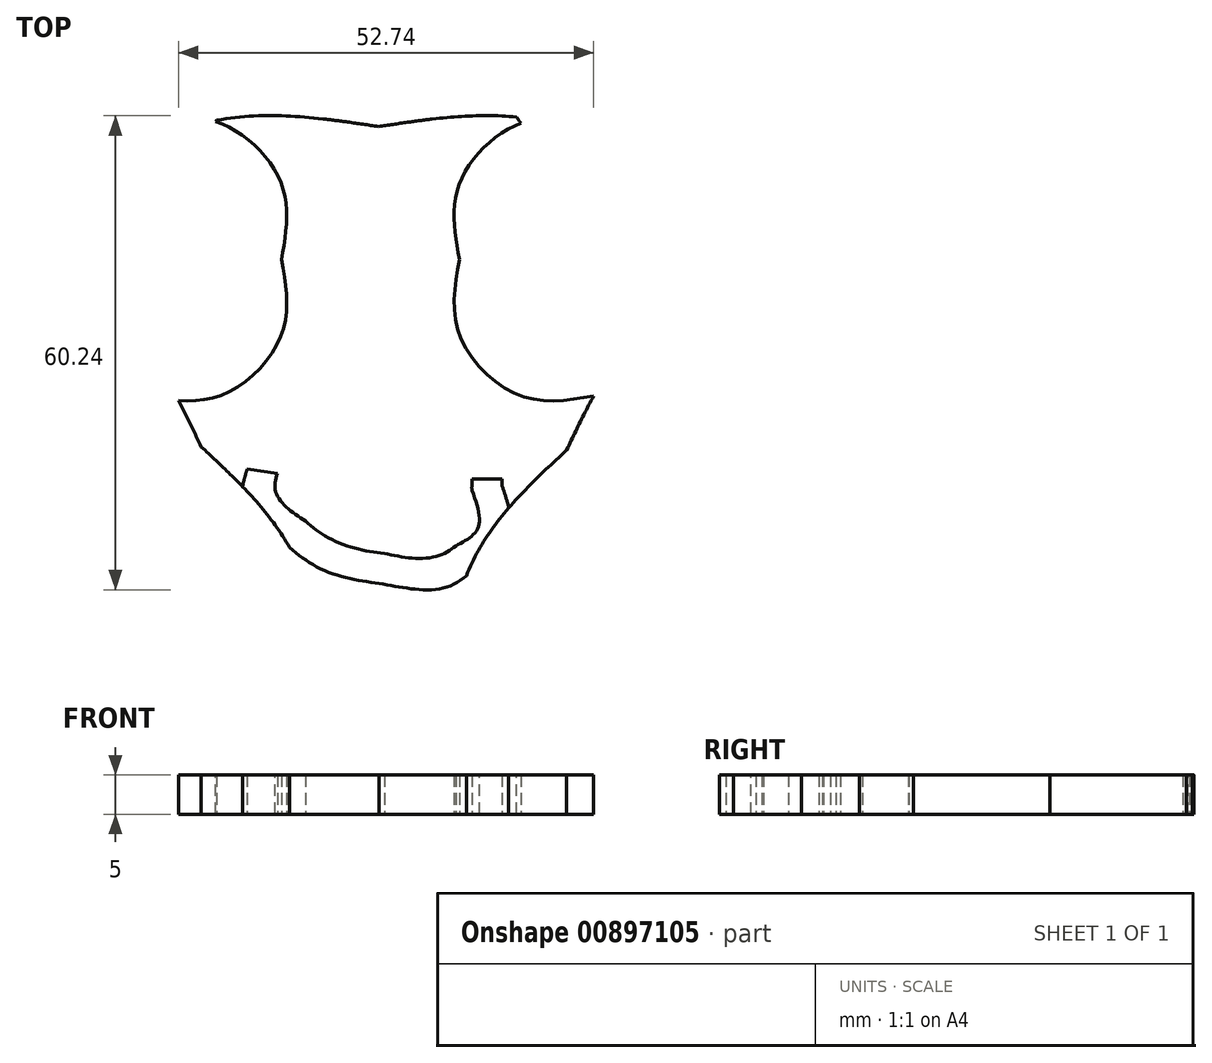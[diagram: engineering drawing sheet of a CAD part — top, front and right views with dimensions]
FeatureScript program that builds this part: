
annotation { "Feature Type Name" : "Feature", "Feature Type Description" : "" }
export const myFeature = defineFeature(function(context is Context, id is Id, definition is map)
    precondition{}
    {
        {
            var Q0;
            Q0=qCreatedBy(makeId("Top.planeOp"),FACE);
            var sketch = newSketch(context, id + "F0", { "sketchPlane" : qUnion([Q0])});
            skLineSegment(sketch, "E0", {"start": v(-46.86, -8.88) * mm, "end": v(-46.86, -8.8) * mm});
            skLineSegment(sketch, "E1", {"start": v(-65.14, 32.5) * mm, "end": v(-66.9, 31.52) * mm});
            skLineSegment(sketch, "E2", {"start": v(-116.84, 62) * mm, "end": v(-116.62, 62.31) * mm});
            skLineSegment(sketch, "E3", {"start": v(-116.62, 62.31) * mm, "end": v(-116.84, 62) * mm});
            skLineSegment(sketch, "E4", {"start": v(-68.87, 38.19) * mm, "end": v(-85.8, 24.7) * mm});
            skLineSegment(sketch, "E5", {"start": v(-85.8, 24.7) * mm, "end": v(-81.78, 19.66) * mm});
            skLineSegment(sketch, "E6", {"start": v(-81.78, 19.66) * mm, "end": v(-66.9, 31.52) * mm});
            skLineSegment(sketch, "E7", {"start": v(16.61, -28.9) * mm, "end": v(16.61, -28.02) * mm});
            skLineSegment(sketch, "E8", {"start": v(16.61, -28.02) * mm, "end": v(12.75, -28.02) * mm});
            skLineSegment(sketch, "E9", {"start": v(-11.95, -27.29) * mm, "end": v(-15.77, -26.73) * mm});
            skLineSegment(sketch, "E10", {"start": v(-15.77, -26.73) * mm, "end": v(-11.95, -27.29) * mm});
            skLineSegment(sketch, "E11", {"start": v(-14.67, 45.1) * mm, "end": v(-11.05, 44.39) * mm});
            skLineSegment(sketch, "E12", {"start": v(-11.05, 44.39) * mm, "end": v(-10.47, 47.34) * mm});
            skLineSegment(sketch, "E13", {"start": v(-10.47, 47.34) * mm, "end": v(-12, 47.64) * mm});
            skLineSegment(sketch, "E14", {"start": v(-12, 47.64) * mm, "end": v(-9.9, 51.16) * mm});
            skLineSegment(sketch, "E15", {"start": v(-9.9, 51.16) * mm, "end": v(-7.44, 45.28) * mm});
            skLineSegment(sketch, "E16", {"start": v(-4.7, 46.53) * mm, "end": v(-4.66, 46.45) * mm});
            skLineSegment(sketch, "E17", {"start": v(-4.66, 46.45) * mm, "end": v(-4.7, 46.53) * mm});
            skLineSegment(sketch, "E18", {"start": v(9.82, 55.07) * mm, "end": v(6.2, 46.45) * mm});
            skLineSegment(sketch, "E19", {"start": v(6.2, 46.45) * mm, "end": v(6.23, 46.53) * mm});
            skLineSegment(sketch, "E20", {"start": v(6.23, 46.53) * mm, "end": v(9.82, 55.07) * mm});
            skLineSegment(sketch, "E21", {"start": v(8.97, 45.28) * mm, "end": v(11.44, 51.16) * mm});
            skLineSegment(sketch, "E22", {"start": v(11.44, 51.16) * mm, "end": v(13.53, 47.64) * mm});
            skLineSegment(sketch, "E23", {"start": v(13.53, 47.64) * mm, "end": v(12, 47.34) * mm});
            skLineSegment(sketch, "E24", {"start": v(12, 47.34) * mm, "end": v(12.58, 44.39) * mm});
            skLineSegment(sketch, "E25", {"start": v(12.58, 44.39) * mm, "end": v(16.2, 45.1) * mm});
            skLineSegment(sketch, "E26", {"start": v(17.2, 47.34) * mm, "end": v(12.5, 55.26) * mm});
            skLineSegment(sketch, "E27", {"start": v(12.5, 55.26) * mm, "end": v(17.2, 47.34) * mm});
            skLineSegment(sketch, "E28", {"start": v(-1.94, -75.4) * mm, "end": v(-1.94, -72.82) * mm});
            skLineSegment(sketch, "E29", {"start": v(-1.94, -72.82) * mm, "end": v(-1.22, -72.82) * mm});
            skLineSegment(sketch, "E30", {"start": v(-1.22, -72.82) * mm, "end": v(-6.78, -63.6) * mm});
            skLineSegment(sketch, "E31", {"start": v(-6.78, -63.6) * mm, "end": v(-6.78, -52.79) * mm});
            skLineSegment(sketch, "E32", {"start": v(4.46, -64.66) * mm, "end": v(10.59, -74.82) * mm});
            skLineSegment(sketch, "E33", {"start": v(11.69, -75.44) * mm, "end": v(11.69, -72.85) * mm});
            skLineSegment(sketch, "E34", {"start": v(11.69, -72.85) * mm, "end": v(12.4, -72.85) * mm});
            skLineSegment(sketch, "E35", {"start": v(12.4, -72.85) * mm, "end": v(6.84, -63.62) * mm});
            skLineSegment(sketch, "E36", {"start": v(6.84, -63.62) * mm, "end": v(6.84, -52.78) * mm});
            skLineSegment(sketch, "E37", {"start": v(59.65, 56.98) * mm, "end": v(70.61, 49.4) * mm});
            skLineSegment(sketch, "E38", {"start": v(60.06, 58.77) * mm, "end": v(60.06, 58.77) * mm});
            skLineSegment(sketch, "E39", {"start": v(73.56, 1.7) * mm, "end": v(73.56, 1.7) * mm});
            skLineSegment(sketch, "E40", {"start": v(84.95, 53.47) * mm, "end": v(62.16, 63) * mm});
            skLineSegment(sketch, "E41", {"start": v(62.16, 63) * mm, "end": v(59.65, 56.98) * mm});
            skLineSegment(sketch, "E42", {"start": v(87.28, 80.72) * mm, "end": v(87.28, 80.72) * mm});
            skLineSegment(sketch, "E43", {"start": v(121.59, 54.04) * mm, "end": v(121.59, 54.04) * mm});
            skLineSegment(sketch, "E44", {"start": v(118.71, 67.05) * mm, "end": v(118.71, 67.05) * mm});
            skLineSegment(sketch, "E45", {"start": v(110.57, 61.37) * mm, "end": v(110.57, 61.37) * mm});
            skFitSpline(sketch, "E46", {"points": [v(-34.7, -84.65) * mm, v(-55.4, -99.81) * mm, v(-83.07, -97.2) * mm, v(-96.56, -78.78) * mm]});
            skFitSpline(sketch, "E47", {"points": [v(-96.56, -78.78) * mm, v(-110, -60.4) * mm, v(-104.14, -33.21) * mm, v(-83.45, -18.08) * mm]});
            skFitSpline(sketch, "E48", {"points": [v(-21.63, -23.91) * mm, v(-8.14, -42.33) * mm, v(-14, -69.52) * mm, v(-34.7, -84.65) * mm]});
            skFitSpline(sketch, "E49", {"points": [v(-83.45, -18.08) * mm, v(-62.8, -2.92) * mm, v(-35.08, -5.53) * mm, v(-21.63, -23.91) * mm]});
            skFitSpline(sketch, "E50", {"points": [v(-29.88, 7.13) * mm, v(-46.62, -15.73) * mm, v(-81.06, -18.98) * mm, v(-106.76, -0.16) * mm]});
            skFitSpline(sketch, "E51", {"points": [v(-46.13, 82.62) * mm, v(-20.4, 63.8) * mm, v(-13.11, 29.99) * mm, v(-29.88, 7.13) * mm]});
            skFitSpline(sketch, "E52", {"points": [v(-106.76, -0.16) * mm, v(-132.5, 18.67) * mm, v(-139.78, 52.51) * mm, v(-123.04, 75.37) * mm]});
            skFitSpline(sketch, "E53", {"points": [v(-123.04, 75.37) * mm, v(-106.27, 98.23) * mm, v(-71.87, 101.48) * mm, v(-46.13, 82.62) * mm]});
            skFitSpline(sketch, "E54", {"points": [v(-69.89, 59.6) * mm, v(-60.89, 70.55) * mm, v(-45.8, 73.02) * mm, v(-36.16, 65.06) * mm]});
            skFitSpline(sketch, "E55", {"points": [v(-36.16, 65.06) * mm, v(-26.48, 57.14) * mm, v(-25.92, 41.87) * mm, v(-34.93, 30.92) * mm]});
            skFitSpline(sketch, "E56", {"points": [v(-34.93, 30.92) * mm, v(-43.9, 19.98) * mm, v(-58.98, 17.55) * mm, v(-68.66, 25.47) * mm]});
            skFitSpline(sketch, "E57", {"points": [v(-78, 61.63) * mm, v(-69, 72.57) * mm, v(-53.86, 75) * mm, v(-44.23, 67.08) * mm]});
            skFitSpline(sketch, "E58", {"points": [v(-44.23, 67.08) * mm, v(-34.55, 59.16) * mm, v(-34, 43.85) * mm, v(-43, 32.9) * mm]});
            skFitSpline(sketch, "E59", {"points": [v(-43, 32.9) * mm, v(-51.96, 21.96) * mm, v(-67.09, 19.53) * mm, v(-76.72, 27.45) * mm]});
            skFitSpline(sketch, "E60", {"points": [v(-82.96, 36.67) * mm, v(-91.85, 36.67) * mm, v(-99.06, 43.73) * mm, v(-99.06, 52.47) * mm]});
            skFitSpline(sketch, "E61", {"points": [v(-99.06, 52.47) * mm, v(-99.06, 61.22) * mm, v(-91.85, 68.28) * mm, v(-82.96, 68.28) * mm]});
            skFitSpline(sketch, "E62", {"points": [v(-82.96, 68.28) * mm, v(-74.07, 68.28) * mm, v(-66.86, 61.22) * mm, v(-66.86, 52.47) * mm]});
            skFitSpline(sketch, "E63", {"points": [v(-66.86, 52.47) * mm, v(-66.86, 43.73) * mm, v(-74.07, 36.67) * mm, v(-82.96, 36.67) * mm]});
            skFitSpline(sketch, "E64", {"points": [v(-82.96, 36.67) * mm, v(-91.85, 36.67) * mm, v(-99.06, 43.73) * mm, v(-99.06, 52.47) * mm]});
            skFitSpline(sketch, "E65", {"points": [v(-99.06, 52.47) * mm, v(-99.06, 61.22) * mm, v(-91.85, 68.28) * mm, v(-82.96, 68.28) * mm]});
            skFitSpline(sketch, "E66", {"points": [v(-82.96, 68.28) * mm, v(-74.07, 68.28) * mm, v(-66.86, 61.22) * mm, v(-66.86, 52.47) * mm]});
            skFitSpline(sketch, "E67", {"points": [v(-66.86, 52.47) * mm, v(-66.86, 43.73) * mm, v(-74.07, 36.67) * mm, v(-82.96, 36.67) * mm]});
            skFitSpline(sketch, "E68", {"points": [v(-75.8, 43.55) * mm, v(-79.11, 40.82) * mm, v(-84.08, 41.34) * mm, v(-86.88, 44.74) * mm]});
            skFitSpline(sketch, "E69", {"points": [v(-86.88, 44.74) * mm, v(-89.69, 48.14) * mm, v(-89.24, 53.1) * mm, v(-85.88, 55.84) * mm]});
            skFitSpline(sketch, "E70", {"points": [v(-85.88, 55.84) * mm, v(-82.55, 58.56) * mm, v(-77.58, 58.04) * mm, v(-74.82, 54.64) * mm]});
            skFitSpline(sketch, "E71", {"points": [v(-74.82, 54.64) * mm, v(-72.02, 51.24) * mm, v(-72.47, 46.27) * mm, v(-75.8, 43.55) * mm]});
            skFitSpline(sketch, "E72", {"points": [v(-75.8, 43.55) * mm, v(-79.11, 40.82) * mm, v(-84.08, 41.34) * mm, v(-86.88, 44.74) * mm]});
            skFitSpline(sketch, "E73", {"points": [v(-86.88, 44.74) * mm, v(-89.69, 48.14) * mm, v(-89.24, 53.1) * mm, v(-85.88, 55.84) * mm]});
            skFitSpline(sketch, "E74", {"points": [v(-85.88, 55.84) * mm, v(-82.55, 58.56) * mm, v(-77.58, 58.04) * mm, v(-74.82, 54.64) * mm]});
            skFitSpline(sketch, "E75", {"points": [v(-74.82, 54.64) * mm, v(-72.02, 51.24) * mm, v(-72.47, 46.27) * mm, v(-75.8, 43.55) * mm]});
            skFitSpline(sketch, "E76", {"points": [v(-102.83, 35.67) * mm, v(-109.7, 45.94) * mm, v(-117.51, 49.97) * mm, v(-109.3, 60.13) * mm]});
            skFitSpline(sketch, "E77", {"points": [v(-109.3, 60.13) * mm, v(-101.45, 69.73) * mm, v(-97.08, 80.04) * mm, v(-86.17, 81.76) * mm]});
            skFitSpline(sketch, "E78", {"points": [v(-56.55, 65.4) * mm, v(-57.45, 57.4) * mm, v(-54.76, 40.52) * mm, v(-65.14, 32.5) * mm]});
            skFitSpline(sketch, "E79", {"points": [v(-85.17, 83.6) * mm, v(-98.56, 83.6) * mm, v(-109.03, 74.4) * mm, v(-116.84, 62) * mm]});
            skFitSpline(sketch, "E80", {"points": [v(-116.62, 62.31) * mm, v(-119.13, 59.22) * mm, v(-120.2, 55.6) * mm, v(-120.12, 52.12) * mm]});
            skFitSpline(sketch, "E81", {"points": [v(-120.12, 52.12) * mm, v(-120.03, 48.64) * mm, v(-118.92, 45.3) * mm, v(-117.4, 42.11) * mm]});
            skFitSpline(sketch, "E82", {"points": [v(-117.4, 42.11) * mm, v(-114.34, 35.74) * mm, v(-109.54, 29.77) * mm, v(-106.22, 24.8) * mm]});
            skFitSpline(sketch, "E83", {"points": [v(-106.22, 24.8) * mm, v(-106.22, 24.8) * mm, v(-106.22, 24.8) * mm, v(-106.22, 24.8) * mm]});
            skFitSpline(sketch, "E84", {"points": [v(-106.22, 24.8) * mm, v(-100.9, 16.85) * mm, v(-91.9, 13.25) * mm, v(-82.78, 10.18) * mm]});
            skFitSpline(sketch, "E85", {"points": [v(-82.78, 10.18) * mm, v(-73.66, 7.1) * mm, v(-64.16, 4.52) * mm, v(-57, -0.26) * mm]});
            skFitSpline(sketch, "E86", {"points": [v(-53.42, 5.1) * mm, v(-61.83, 10.71) * mm, v(-71.89, 13.31) * mm, v(-80.73, 16.28) * mm]});
            skFitSpline(sketch, "E87", {"points": [v(-111.39, 58.56) * mm, v(-104.23, 69.93) * mm, v(-95.72, 77.05) * mm, v(-85.37, 77.15) * mm]});
            skFitSpline(sketch, "E88", {"points": [v(-85.37, 77.15) * mm, v(-79.56, 76.37) * mm, v(-73.73, 74.84) * mm, v(-69.2, 72.53) * mm]});
            skFitSpline(sketch, "E89", {"points": [v(-69.2, 72.53) * mm, v(-64.8, 70.28) * mm, v(-61.79, 67.42) * mm, v(-60.52, 63.9) * mm]});
            skFitSpline(sketch, "E90", {"points": [v(-60.52, 63.9) * mm, v(-61.3, 55.24) * mm, v(-60.15, 44.93) * mm, v(-68.83, 38.22) * mm]});
            skFitSpline(sketch, "E91", {"points": [v(-68.83, 38.22) * mm, v(-68.85, 38.2) * mm, v(-68.86, 38.2) * mm, v(-68.87, 38.19) * mm]});
            skFitSpline(sketch, "E92", {"points": [v(-64.9, 33.12) * mm, v(-53.08, 42.25) * mm, v(-54.83, 56.8) * mm, v(-54.06, 64.05) * mm]});
            skFitSpline(sketch, "E93", {"points": [v(-54.06, 64.05) * mm, v(-54.01, 64.48) * mm, v(-54.06, 64.93) * mm, v(-54.19, 65.34) * mm]});
            skFitSpline(sketch, "E94", {"points": [v(-54.19, 65.34) * mm, v(-56.02, 71.25) * mm, v(-60.72, 75.43) * mm, v(-66.26, 78.26) * mm]});
            skFitSpline(sketch, "E95", {"points": [v(-66.26, 78.26) * mm, v(-71.8, 81.1) * mm, v(-78.34, 82.73) * mm, v(-84.75, 83.57) * mm]});
            skFitSpline(sketch, "E96", {"points": [v(-84.75, 83.57) * mm, v(-84.89, 83.6) * mm, v(-85.03, 83.6) * mm, v(-85.17, 83.6) * mm]});
            skFitSpline(sketch, "E97", {"points": [v(-58.53, -0.23) * mm, v(-63.17, 2.42) * mm, v(-66, 6.12) * mm, v(-64.92, 8.02) * mm]});
            skFitSpline(sketch, "E98", {"points": [v(-64.92, 8.02) * mm, v(-63.8, 9.9) * mm, v(-59.2, 9.3) * mm, v(-54.57, 6.64) * mm]});
            skFitSpline(sketch, "E99", {"points": [v(-54.57, 6.64) * mm, v(-49.98, 3.95) * mm, v(-47.1, 0.3) * mm, v(-48.22, -1.61) * mm]});
            skFitSpline(sketch, "E100", {"points": [v(-48.22, -1.61) * mm, v(-49.3, -3.52) * mm, v(-53.94, -2.88) * mm, v(-58.53, -0.23) * mm]});
            skFitSpline(sketch, "E101", {"points": [v(24.8, -24.32) * mm, v(38.29, -5.9) * mm, v(65.96, -3.26) * mm, v(86.66, -18.42) * mm]});
            skFitSpline(sketch, "E102", {"points": [v(86.66, -18.42) * mm, v(107.31, -33.55) * mm, v(113.18, -60.78) * mm, v(99.7, -79.16) * mm]});
            skFitSpline(sketch, "E103", {"points": [v(99.7, -79.16) * mm, v(86.2, -97.57) * mm, v(58.53, -100.19) * mm, v(37.84, -85.06) * mm]});
            skFitSpline(sketch, "E104", {"points": [v(37.84, -85.06) * mm, v(17.18, -69.9) * mm, v(11.32, -42.7) * mm, v(24.8, -24.32) * mm]});
            skFitSpline(sketch, "E105", {"points": [v(0.9, -52.41) * mm, v(-23.01, -52.41) * mm, v(-42.36, -36.95) * mm, v(-42.36, -17.82) * mm]});
            skFitSpline(sketch, "E106", {"points": [v(-42.36, -17.82) * mm, v(-42.36, 1.26) * mm, v(-23.01, 16.77) * mm, v(0.9, 16.77) * mm]});
            skFitSpline(sketch, "E107", {"points": [v(0.9, 16.77) * mm, v(24.8, 16.77) * mm, v(44.15, 1.26) * mm, v(44.15, -17.82) * mm]});
            skFitSpline(sketch, "E108", {"points": [v(44.15, -17.82) * mm, v(44.15, -36.95) * mm, v(24.8, -52.41) * mm, v(0.9, -52.41) * mm]});
            skFitSpline(sketch, "E109", {"points": [v(-28.76, -17.41) * mm, v(-38.33, -17.41) * mm, v(-46.06, -9.64) * mm, v(-46.06, -0.12) * mm]});
            skFitSpline(sketch, "E110", {"points": [v(-46.06, -0.12) * mm, v(-46.06, 9.44) * mm, v(-38.33, 17.18) * mm, v(-28.76, 17.18) * mm]});
            skFitSpline(sketch, "E111", {"points": [v(-28.76, 17.18) * mm, v(-19.2, 17.18) * mm, v(-11.43, 9.44) * mm, v(-11.43, -0.12) * mm]});
            skFitSpline(sketch, "E112", {"points": [v(-11.43, -0.12) * mm, v(-11.43, -9.64) * mm, v(-19.2, -17.41) * mm, v(-28.76, -17.41) * mm]});
            skFitSpline(sketch, "E113", {"points": [v(-28.76, 15.67) * mm, v(-20.01, 15.67) * mm, v(-12.94, 8.63) * mm, v(-12.94, -0.12) * mm]});
            skFitSpline(sketch, "E114", {"points": [v(-12.94, -0.12) * mm, v(-12.94, -8.82) * mm, v(-20.02, -15.9) * mm, v(-28.76, -15.9) * mm]});
            skFitSpline(sketch, "E115", {"points": [v(-28.76, -15.9) * mm, v(-37.51, -15.9) * mm, v(-44.55, -8.83) * mm, v(-44.55, -0.12) * mm]});
            skFitSpline(sketch, "E116", {"points": [v(-44.55, -0.12) * mm, v(-44.55, 8.63) * mm, v(-37.51, 15.67) * mm, v(-28.76, 15.67) * mm]});
            skFitSpline(sketch, "E117", {"points": [v(30.55, 5) * mm, v(13.9, 27.7) * mm, v(21.14, 61.3) * mm, v(46.7, 80.04) * mm]});
            skFitSpline(sketch, "E118", {"points": [v(106.94, -2.25) * mm, v(81.4, -20.96) * mm, v(47.18, -17.71) * mm, v(30.55, 5) * mm]});
            skFitSpline(sketch, "E119", {"points": [v(30.55, 5) * mm, v(13.9, 27.7) * mm, v(21.14, 61.3) * mm, v(46.7, 80.04) * mm]});
            skFitSpline(sketch, "E120", {"points": [v(46.7, 80.04) * mm, v(72.24, 98.76) * mm, v(106.45, 95.5) * mm, v(123.08, 72.8) * mm]});
            skFitSpline(sketch, "E121", {"points": [v(123.08, 72.8) * mm, v(139.74, 50.05) * mm, v(132.49, 16.47) * mm, v(106.94, -2.25) * mm]});
            skFitSpline(sketch, "E122", {"points": [v(113.78, 46.24) * mm, v(122.7, 35.37) * mm, v(122.18, 20.16) * mm, v(112.58, 12.28) * mm]});
            skFitSpline(sketch, "E123", {"points": [v(112.58, 12.28) * mm, v(102.98, 4.4) * mm, v(87.96, 6.87) * mm, v(79.04, 17.74) * mm]});
            skFitSpline(sketch, "E124", {"points": [v(104.59, 12.28) * mm, v(94.99, 4.4) * mm, v(79.97, 6.87) * mm, v(71.04, 17.74) * mm]});
            skFitSpline(sketch, "E125", {"points": [v(71.04, 17.74) * mm, v(62.12, 28.6) * mm, v(62.64, 43.8) * mm, v(72.24, 51.65) * mm]});
            skFitSpline(sketch, "E126", {"points": [v(71.04, 17.74) * mm, v(62.12, 28.6) * mm, v(62.64, 43.8) * mm, v(72.24, 51.65) * mm]});
            skFitSpline(sketch, "E127", {"points": [v(105.78, 46.24) * mm, v(114.7, 35.37) * mm, v(114.15, 20.16) * mm, v(104.59, 12.28) * mm]});
            skFitSpline(sketch, "E128", {"points": [v(64.28, 16.06) * mm, v(56.44, 16.06) * mm, v(50.13, 22.48) * mm, v(50.13, 30.44) * mm]});
            skFitSpline(sketch, "E129", {"points": [v(50.13, 30.44) * mm, v(50.13, 38.4) * mm, v(56.44, 44.82) * mm, v(64.28, 44.82) * mm]});
            skFitSpline(sketch, "E130", {"points": [v(64.28, 44.82) * mm, v(72.09, 44.82) * mm, v(78.4, 38.4) * mm, v(78.4, 30.44) * mm]});
            skFitSpline(sketch, "E131", {"points": [v(78.4, 30.44) * mm, v(78.4, 22.48) * mm, v(72.09, 16.06) * mm, v(64.28, 16.06) * mm]});
            skFitSpline(sketch, "E132", {"points": [v(64.28, 16.06) * mm, v(56.44, 16.06) * mm, v(50.13, 22.48) * mm, v(50.13, 30.44) * mm]});
            skFitSpline(sketch, "E133", {"points": [v(50.13, 30.44) * mm, v(50.13, 38.4) * mm, v(56.44, 44.82) * mm, v(64.28, 44.82) * mm]});
            skFitSpline(sketch, "E134", {"points": [v(64.28, 44.82) * mm, v(72.09, 44.82) * mm, v(78.4, 38.4) * mm, v(78.4, 30.44) * mm]});
            skFitSpline(sketch, "E135", {"points": [v(78.4, 30.44) * mm, v(78.4, 22.48) * mm, v(72.09, 16.06) * mm, v(64.28, 16.06) * mm]});
            skFitSpline(sketch, "E136", {"points": [v(69.25, 22.18) * mm, v(65.93, 19.5) * mm, v(61, 20.02) * mm, v(58.23, 23.41) * mm]});
            skFitSpline(sketch, "E137", {"points": [v(58.23, 23.41) * mm, v(55.47, 26.78) * mm, v(55.88, 31.74) * mm, v(59.17, 34.43) * mm]});
            skFitSpline(sketch, "E138", {"points": [v(59.17, 34.43) * mm, v(62.45, 37.16) * mm, v(67.42, 36.6) * mm, v(70.18, 33.24) * mm]});
            skFitSpline(sketch, "E139", {"points": [v(70.18, 33.24) * mm, v(72.95, 29.84) * mm, v(72.54, 24.9) * mm, v(69.25, 22.18) * mm]});
            skFitSpline(sketch, "E140", {"points": [v(69.25, 22.18) * mm, v(65.93, 19.5) * mm, v(61, 20.02) * mm, v(58.23, 23.41) * mm]});
            skFitSpline(sketch, "E141", {"points": [v(58.23, 23.41) * mm, v(55.47, 26.78) * mm, v(55.88, 31.74) * mm, v(59.17, 34.43) * mm]});
            skFitSpline(sketch, "E142", {"points": [v(59.17, 34.43) * mm, v(62.45, 37.16) * mm, v(67.42, 36.6) * mm, v(70.18, 33.24) * mm]});
            skFitSpline(sketch, "E143", {"points": [v(70.18, 33.24) * mm, v(72.95, 29.84) * mm, v(72.54, 24.9) * mm, v(69.25, 22.18) * mm]});
            skFitSpline(sketch, "E144", {"points": [v(28.5, -17.41) * mm, v(18.94, -17.41) * mm, v(11.17, -9.64) * mm, v(11.17, -0.12) * mm]});
            skFitSpline(sketch, "E145", {"points": [v(11.17, -0.12) * mm, v(11.17, 9.44) * mm, v(18.94, 17.18) * mm, v(28.5, 17.18) * mm]});
            skFitSpline(sketch, "E146", {"points": [v(28.5, 17.18) * mm, v(38.06, 17.18) * mm, v(45.8, 9.44) * mm, v(45.8, -0.12) * mm]});
            skFitSpline(sketch, "E147", {"points": [v(45.8, -0.12) * mm, v(45.8, -9.64) * mm, v(38.06, -17.41) * mm, v(28.5, -17.41) * mm]});
            skFitSpline(sketch, "E148", {"points": [v(47.3, -0.12) * mm, v(47.3, 10.26) * mm, v(38.87, 18.68) * mm, v(28.5, 18.68) * mm]});
            skFitSpline(sketch, "E149", {"points": [v(28.5, 15.67) * mm, v(37.25, 15.67) * mm, v(44.29, 8.63) * mm, v(44.29, -0.12) * mm]});
            skFitSpline(sketch, "E150", {"points": [v(44.29, -0.12) * mm, v(44.29, -8.83) * mm, v(37.25, -15.9) * mm, v(28.5, -15.9) * mm]});
            skFitSpline(sketch, "E151", {"points": [v(28.5, -15.9) * mm, v(19.75, -15.9) * mm, v(12.67, -8.82) * mm, v(12.67, -0.12) * mm]});
            skFitSpline(sketch, "E152", {"points": [v(12.67, -0.12) * mm, v(12.67, 8.63) * mm, v(19.75, 15.67) * mm, v(28.5, 15.67) * mm]});
            skFitSpline(sketch, "E153", {"points": [v(-28.24, -8.7) * mm, v(-33.02, -8.7) * mm, v(-36.9, -4.82) * mm, v(-36.9, -0.04) * mm]});
            skFitSpline(sketch, "E154", {"points": [v(-36.9, -0.04) * mm, v(-36.9, 4.74) * mm, v(-33.02, 8.62) * mm, v(-28.24, 8.62) * mm]});
            skFitSpline(sketch, "E155", {"points": [v(-28.24, 8.62) * mm, v(-23.46, 8.62) * mm, v(-19.61, 4.74) * mm, v(-19.61, -0.04) * mm]});
            skFitSpline(sketch, "E156", {"points": [v(-19.61, -0.04) * mm, v(-19.61, -4.82) * mm, v(-23.46, -8.7) * mm, v(-28.24, -8.7) * mm]});
            skFitSpline(sketch, "E157", {"points": [v(-28.24, -8.7) * mm, v(-33.02, -8.7) * mm, v(-36.9, -4.82) * mm, v(-36.9, -0.04) * mm]});
            skFitSpline(sketch, "E158", {"points": [v(-36.9, -0.04) * mm, v(-36.9, 4.74) * mm, v(-33.02, 8.62) * mm, v(-28.24, 8.62) * mm]});
            skFitSpline(sketch, "E159", {"points": [v(-28.24, 8.62) * mm, v(-23.46, 8.62) * mm, v(-19.61, 4.74) * mm, v(-19.61, -0.04) * mm]});
            skFitSpline(sketch, "E160", {"points": [v(-19.61, -0.04) * mm, v(-19.61, -4.82) * mm, v(-23.46, -8.7) * mm, v(-28.24, -8.7) * mm]});
            skFitSpline(sketch, "E161", {"points": [v(29.13, -7.74) * mm, v(24.32, -7.74) * mm, v(20.47, -3.85) * mm, v(20.47, 0.9) * mm]});
            skFitSpline(sketch, "E162", {"points": [v(20.47, 0.9) * mm, v(20.47, 5.67) * mm, v(24.32, 9.52) * mm, v(29.13, 9.52) * mm]});
            skFitSpline(sketch, "E163", {"points": [v(29.13, 9.52) * mm, v(33.92, 9.52) * mm, v(37.76, 5.67) * mm, v(37.76, 0.9) * mm]});
            skFitSpline(sketch, "E164", {"points": [v(37.76, 0.9) * mm, v(37.76, -3.85) * mm, v(33.92, -7.74) * mm, v(29.13, -7.74) * mm]});
            skFitSpline(sketch, "E165", {"points": [v(29.13, -7.74) * mm, v(24.32, -7.74) * mm, v(20.47, -3.85) * mm, v(20.47, 0.9) * mm]});
            skFitSpline(sketch, "E166", {"points": [v(20.47, 0.9) * mm, v(20.47, 5.67) * mm, v(24.32, 9.52) * mm, v(29.13, 9.52) * mm]});
            skFitSpline(sketch, "E167", {"points": [v(29.13, 9.52) * mm, v(33.92, 9.52) * mm, v(37.76, 5.67) * mm, v(37.76, 0.9) * mm]});
            skFitSpline(sketch, "E168", {"points": [v(37.76, 0.9) * mm, v(37.76, -3.85) * mm, v(33.92, -7.74) * mm, v(29.13, -7.74) * mm]});
            skFitSpline(sketch, "E169", {"points": [v(-15.77, -26.73) * mm, v(-16.34, -30.63) * mm, v(-13.93, -34.04) * mm, v(-10.7, -36.46) * mm]});
            skFitSpline(sketch, "E170", {"points": [v(-10.7, -36.46) * mm, v(-7.46, -38.87) * mm, v(-3.23, -40.55) * mm, v(1, -41.26) * mm]});
            skFitSpline(sketch, "E171", {"points": [v(1, -41.26) * mm, v(5.23, -41.97) * mm, v(9.48, -41.77) * mm, v(12.73, -39.78) * mm]});
            skFitSpline(sketch, "E172", {"points": [v(12.73, -39.78) * mm, v(15.92, -37.84) * mm, v(17.63, -33.88) * mm, v(16.61, -28.9) * mm]});
            skFitSpline(sketch, "E173", {"points": [v(12.75, -28.02) * mm, v(12.75, -28.02) * mm, v(12.75, -28.02) * mm, v(12.75, -28.07) * mm, v(12.75, -28.98) * mm, v(12.75, -29.03) * mm, v(12.75, -29.03) * mm, v(12.75, -29.03) * mm]});
            skFitSpline(sketch, "E174", {"points": [v(12.75, -29.03) * mm, v(12.75, -29.17) * mm, v(12.76, -29.31) * mm, v(12.8, -29.45) * mm]});
            skFitSpline(sketch, "E175", {"points": [v(12.8, -29.45) * mm, v(13.71, -33.52) * mm, v(12.7, -35.27) * mm, v(10.72, -36.48) * mm]});
            skFitSpline(sketch, "E176", {"points": [v(10.72, -36.48) * mm, v(8.74, -37.7) * mm, v(5.28, -38.06) * mm, v(1.64, -37.45) * mm]});
            skFitSpline(sketch, "E177", {"points": [v(1.64, -37.45) * mm, v(-2, -36.84) * mm, v(-5.78, -35.3) * mm, v(-8.39, -33.36) * mm]});
            skFitSpline(sketch, "E178", {"points": [v(-8.39, -33.36) * mm, v(-10.99, -31.41) * mm, v(-12.24, -29.31) * mm, v(-11.95, -27.29) * mm]});
            skFitSpline(sketch, "E179", {"points": [v(-9.72, 56) * mm, v(-10.23, 55.98) * mm, v(-10.7, 55.7) * mm, v(-10.97, 55.26) * mm]});
            skFitSpline(sketch, "E180", {"points": [v(-10.97, 55.26) * mm, v(-10.97, 55.26) * mm, v(-10.97, 55.26) * mm, v(-11.09, 55.06) * mm, v(-15.56, 47.54) * mm, v(-15.67, 47.34) * mm, v(-15.67, 47.34) * mm, v(-15.68, 47.34) * mm]});
            skFitSpline(sketch, "E181", {"points": [v(-15.68, 47.34) * mm, v(-15.93, 46.92) * mm, v(-15.96, 46.4) * mm, v(-15.76, 45.96) * mm]});
            skFitSpline(sketch, "E182", {"points": [v(-15.76, 45.96) * mm, v(-15.56, 45.51) * mm, v(-15.15, 45.2) * mm, v(-14.67, 45.1) * mm]});
            skFitSpline(sketch, "E183", {"points": [v(-7.44, 45.28) * mm, v(-7.43, 45.25) * mm, v(-7.42, 45.22) * mm, v(-7.4, 45.2) * mm]});
            skFitSpline(sketch, "E184", {"points": [v(-7.4, 45.2) * mm, v(-3.46, 37.22) * mm, v(-6.73, 26.81) * mm, v(-5.98, 16.95) * mm]});
            skFitSpline(sketch, "E185", {"points": [v(-2.98, 17.18) * mm, v(-3.66, 26.14) * mm, v(-0.05, 37.1) * mm, v(-4.7, 46.53) * mm]});
            skFitSpline(sketch, "E186", {"points": [v(-4.66, 46.45) * mm, v(-4.67, 46.45) * mm, v(-4.67, 46.45) * mm, v(-4.76, 46.67) * mm, v(-8.2, 54.85) * mm, v(-8.29, 55.07) * mm, v(-8.29, 55.07) * mm, v(-8.29, 55.07) * mm]});
            skFitSpline(sketch, "E187", {"points": [v(-8.29, 55.07) * mm, v(-8.53, 55.65) * mm, v(-9.1, 56.01) * mm, v(-9.72, 56) * mm]});
            skFitSpline(sketch, "E188", {"points": [v(11.26, 56) * mm, v(10.63, 56.02) * mm, v(10.06, 55.65) * mm, v(9.82, 55.07) * mm]});
            skFitSpline(sketch, "E189", {"points": [v(6.23, 46.53) * mm, v(1.58, 37.1) * mm, v(5.22, 26.14) * mm, v(4.55, 17.18) * mm]});
            skFitSpline(sketch, "E190", {"points": [v(7.55, 16.95) * mm, v(8.3, 26.82) * mm, v(5, 37.22) * mm, v(8.93, 45.2) * mm]});
            skFitSpline(sketch, "E191", {"points": [v(8.93, 45.2) * mm, v(8.95, 45.22) * mm, v(8.96, 45.25) * mm, v(8.97, 45.28) * mm]});
            skFitSpline(sketch, "E192", {"points": [v(16.2, 45.1) * mm, v(16.68, 45.19) * mm, v(17.09, 45.51) * mm, v(17.29, 45.96) * mm]});
            skFitSpline(sketch, "E193", {"points": [v(17.29, 45.96) * mm, v(17.49, 46.4) * mm, v(17.46, 46.92) * mm, v(17.2, 47.34) * mm]});
            skFitSpline(sketch, "E194", {"points": [v(12.5, 55.26) * mm, v(12.24, 55.7) * mm, v(11.77, 55.98) * mm, v(11.26, 56) * mm]});
            skFitSpline(sketch, "E195", {"points": [v(-80.68, -75.83) * mm, v(-90.62, -67.65) * mm, v(-90.96, -51.63) * mm, v(-81.43, -39.97) * mm]});
            skFitSpline(sketch, "E196", {"points": [v(-81.43, -39.97) * mm, v(-71.87, -28.36) * mm, v(-56.07, -25.56) * mm, v(-46.1, -33.74) * mm]});
            skFitSpline(sketch, "E197", {"points": [v(-46.1, -33.74) * mm, v(-36.16, -41.92) * mm, v(-35.82, -57.94) * mm, v(-45.38, -69.56) * mm]});
            skFitSpline(sketch, "E198", {"points": [v(-45.38, -69.56) * mm, v(-54.91, -81.21) * mm, v(-70.71, -84.01) * mm, v(-80.68, -75.83) * mm]});
            skFitSpline(sketch, "E199", {"points": [v(-80.68, -75.83) * mm, v(-90.62, -67.65) * mm, v(-90.96, -51.63) * mm, v(-81.43, -39.97) * mm]});
            skFitSpline(sketch, "E200", {"points": [v(-81.43, -39.97) * mm, v(-71.87, -28.36) * mm, v(-56.07, -25.56) * mm, v(-46.1, -33.74) * mm]});
            skFitSpline(sketch, "E201", {"points": [v(-46.1, -33.74) * mm, v(-36.16, -41.92) * mm, v(-35.82, -57.94) * mm, v(-45.38, -69.56) * mm]});
            skFitSpline(sketch, "E202", {"points": [v(-45.38, -69.56) * mm, v(-54.91, -81.21) * mm, v(-70.71, -84.01) * mm, v(-80.68, -75.83) * mm]});
            skFitSpline(sketch, "E203", {"points": [v(-9.36, -52.79) * mm, v(-9.36, -52.79) * mm, v(-9.36, -52.79) * mm, v(-9.36, -53.07) * mm, v(-9.36, -63.67) * mm, v(-9.36, -63.95) * mm, v(-9.36, -63.95) * mm, v(-9.36, -63.95) * mm]});
            skFitSpline(sketch, "E204", {"points": [v(-9.36, -63.95) * mm, v(-9.36, -64.19) * mm, v(-9.3, -64.42) * mm, v(-9.17, -64.62) * mm]});
            skFitSpline(sketch, "E205", {"points": [v(-9.17, -64.62) * mm, v(-9.17, -64.62) * mm, v(-9.17, -64.62) * mm, v(-9.1, -64.75) * mm, v(-3.13, -74.65) * mm, v(-3.05, -74.78) * mm, v(-3.05, -74.78) * mm, v(-3.05, -74.78) * mm]});
            skFitSpline(sketch, "E206", {"points": [v(-3.05, -74.78) * mm, v(-2.81, -75.17) * mm, v(-2.4, -75.4) * mm, v(-1.94, -75.4) * mm]});
            skFitSpline(sketch, "E207", {"points": [v(4.27, -52.79) * mm, v(4.27, -52.79) * mm, v(4.27, -52.79) * mm, v(4.27, -53.07) * mm, v(4.27, -63.7) * mm, v(4.27, -63.99) * mm, v(4.27, -63.99) * mm, v(4.27, -64) * mm]});
            skFitSpline(sketch, "E208", {"points": [v(4.27, -64) * mm, v(4.27, -64.23) * mm, v(4.34, -64.46) * mm, v(4.46, -64.66) * mm]});
            skFitSpline(sketch, "E209", {"points": [v(10.59, -74.82) * mm, v(10.82, -75.2) * mm, v(11.24, -75.44) * mm, v(11.69, -75.44) * mm]});
            skFitSpline(sketch, "E210", {"points": [v(-69.03, -62.57) * mm, v(-73.51, -58.91) * mm, v(-72.8, -50.62) * mm, v(-67.42, -44.08) * mm]});
            skFitSpline(sketch, "E211", {"points": [v(-67.42, -44.08) * mm, v(-62.04, -37.5) * mm, v(-54.09, -35.2) * mm, v(-49.57, -38.9) * mm]});
            skFitSpline(sketch, "E212", {"points": [v(-49.57, -38.9) * mm, v(-45.12, -42.55) * mm, v(-45.83, -50.84) * mm, v(-51.17, -57.42) * mm]});
            skFitSpline(sketch, "E213", {"points": [v(-51.17, -57.42) * mm, v(-56.55, -63.95) * mm, v(-64.55, -66.27) * mm, v(-69.03, -62.57) * mm]});
            skFitSpline(sketch, "E214", {"points": [v(-69.03, -62.57) * mm, v(-73.51, -58.91) * mm, v(-72.8, -50.62) * mm, v(-67.42, -44.08) * mm]});
            skFitSpline(sketch, "E215", {"points": [v(-67.42, -44.08) * mm, v(-62.04, -37.5) * mm, v(-54.09, -35.2) * mm, v(-49.57, -38.9) * mm]});
            skFitSpline(sketch, "E216", {"points": [v(-49.57, -38.9) * mm, v(-45.12, -42.55) * mm, v(-45.83, -50.84) * mm, v(-51.17, -57.42) * mm]});
            skFitSpline(sketch, "E217", {"points": [v(-51.17, -57.42) * mm, v(-56.55, -63.95) * mm, v(-64.55, -66.27) * mm, v(-69.03, -62.57) * mm]});
            skFitSpline(sketch, "E218", {"points": [v(81.99, -75.87) * mm, v(72.02, -84.05) * mm, v(56.22, -81.25) * mm, v(46.65, -69.6) * mm]});
            skFitSpline(sketch, "E219", {"points": [v(46.65, -69.6) * mm, v(37.13, -57.98) * mm, v(37.46, -41.92) * mm, v(47.4, -33.77) * mm]});
            skFitSpline(sketch, "E220", {"points": [v(47.4, -33.77) * mm, v(57.37, -25.6) * mm, v(73.17, -28.4) * mm, v(82.74, -40.01) * mm]});
            skFitSpline(sketch, "E221", {"points": [v(82.74, -40.01) * mm, v(92.26, -51.67) * mm, v(91.92, -67.69) * mm, v(81.99, -75.87) * mm]});
            skFitSpline(sketch, "E222", {"points": [v(81.99, -75.87) * mm, v(72.02, -84.05) * mm, v(56.22, -81.25) * mm, v(46.65, -69.6) * mm]});
            skFitSpline(sketch, "E223", {"points": [v(46.65, -69.6) * mm, v(37.13, -57.98) * mm, v(37.46, -41.92) * mm, v(47.4, -33.77) * mm]});
            skFitSpline(sketch, "E224", {"points": [v(47.4, -33.77) * mm, v(57.37, -25.6) * mm, v(73.17, -28.4) * mm, v(82.74, -40.01) * mm]});
            skFitSpline(sketch, "E225", {"points": [v(82.74, -40.01) * mm, v(92.26, -51.67) * mm, v(91.92, -67.69) * mm, v(81.99, -75.87) * mm]});
            skFitSpline(sketch, "E226", {"points": [v(68.99, -63.62) * mm, v(64.5, -67.28) * mm, v(56.51, -64.96) * mm, v(51.17, -58.46) * mm]});
            skFitSpline(sketch, "E227", {"points": [v(51.17, -58.46) * mm, v(45.8, -51.93) * mm, v(45.08, -43.63) * mm, v(49.6, -39.97) * mm]});
            skFitSpline(sketch, "E228", {"points": [v(49.6, -39.97) * mm, v(54.05, -36.28) * mm, v(62.04, -38.6) * mm, v(67.42, -45.13) * mm]});
            skFitSpline(sketch, "E229", {"points": [v(67.42, -45.13) * mm, v(72.76, -51.63) * mm, v(73.47, -59.92) * mm, v(68.99, -63.62) * mm]});
            skFitSpline(sketch, "E230", {"points": [v(68.99, -63.62) * mm, v(64.5, -67.28) * mm, v(56.51, -64.96) * mm, v(51.17, -58.46) * mm]});
            skFitSpline(sketch, "E231", {"points": [v(51.17, -58.46) * mm, v(45.8, -51.93) * mm, v(45.08, -43.63) * mm, v(49.6, -39.97) * mm]});
            skFitSpline(sketch, "E232", {"points": [v(49.6, -39.97) * mm, v(54.05, -36.28) * mm, v(62.04, -38.6) * mm, v(67.42, -45.13) * mm]});
            skFitSpline(sketch, "E233", {"points": [v(67.42, -45.13) * mm, v(72.76, -51.63) * mm, v(73.47, -59.92) * mm, v(68.99, -63.62) * mm]});
            skFitSpline(sketch, "E234", {"points": [v(64.3, 61.6) * mm, v(65.82, 62.59) * mm, v(66.93, 63.32) * mm, v(69.06, 64.74) * mm]});
            skFitSpline(sketch, "E235", {"points": [v(69.06, 64.74) * mm, v(69.06, 64.74) * mm, v(69.06, 64.74) * mm, v(69.06, 64.74) * mm]});
            skFitSpline(sketch, "E236", {"points": [v(69.06, 64.74) * mm, v(73.97, 68.03) * mm, v(84.02, 71.7) * mm, v(92.98, 71.77) * mm]});
            skFitSpline(sketch, "E237", {"points": [v(92.98, 71.77) * mm, v(97.46, 71.8) * mm, v(101.63, 70.99) * mm, v(104.92, 69.12) * mm]});
            skFitSpline(sketch, "E238", {"points": [v(104.92, 69.12) * mm, v(108.2, 67.25) * mm, v(110.73, 64.43) * mm, v(112.2, 59.7) * mm]});
            skFitSpline(sketch, "E239", {"points": [v(70.61, 49.4) * mm, v(75.6, 45.56) * mm, v(80.92, 40.64) * mm, v(84.41, 35.51) * mm]});
            skFitSpline(sketch, "E240", {"points": [v(84.41, 35.51) * mm, v(87.92, 30.37) * mm, v(89.5, 25.35) * mm, v(88.02, 20.6) * mm]});
            skFitSpline(sketch, "E241", {"points": [v(88.02, 20.6) * mm, v(86.65, 16.12) * mm, v(85.64, 14.71) * mm, v(83.78, 13.7) * mm]});
            skFitSpline(sketch, "E242", {"points": [v(83.78, 13.7) * mm, v(81.92, 12.67) * mm, v(78.32, 12.06) * mm, v(72.23, 11.26) * mm]});
            skFitSpline(sketch, "E243", {"points": [v(72.23, 11.26) * mm, v(65.8, 10.4) * mm, v(61.73, 8.95) * mm, v(59.37, 8.87) * mm]});
            skFitSpline(sketch, "E244", {"points": [v(59.37, 8.87) * mm, v(58.2, 8.83) * mm, v(57.46, 8.97) * mm, v(56.4, 9.59) * mm]});
            skFitSpline(sketch, "E245", {"points": [v(56.4, 9.59) * mm, v(55.33, 10.2) * mm, v(53.94, 11.42) * mm, v(52.15, 13.64) * mm]});
            skFitSpline(sketch, "E246", {"points": [v(52.15, 13.64) * mm, v(52.15, 13.64) * mm, v(52.14, 13.64) * mm, v(52.14, 13.64) * mm]});
            skFitSpline(sketch, "E247", {"points": [v(52.14, 13.64) * mm, v(48.35, 18.32) * mm, v(45.63, 23.78) * mm, v(44.66, 29.05) * mm]});
            skFitSpline(sketch, "E248", {"points": [v(44.66, 29.05) * mm, v(43.68, 34.31) * mm, v(44.37, 39.3) * mm, v(47.28, 43.66) * mm]});
            skFitSpline(sketch, "E249", {"points": [v(47.28, 43.66) * mm, v(54.02, 53.76) * mm, v(54.28, 54.84) * mm, v(60.06, 58.77) * mm]});
            skFitSpline(sketch, "E250", {"points": [v(87.28, 80.72) * mm, v(76.71, 80.68) * mm, v(66.63, 78.11) * mm, v(60.73, 74.16) * mm]});
            skFitSpline(sketch, "E251", {"points": [v(60.73, 74.16) * mm, v(45.32, 63.89) * mm, v(46.6, 64.9) * mm, v(37.51, 51.28) * mm]});
            skFitSpline(sketch, "E252", {"points": [v(37.51, 51.28) * mm, v(33.35, 45.05) * mm, v(33.33, 36.97) * mm, v(35.14, 29.29) * mm]});
            skFitSpline(sketch, "E253", {"points": [v(35.14, 29.29) * mm, v(36.95, 21.6) * mm, v(40.67, 14.14) * mm, v(45.12, 8.65) * mm]});
            skFitSpline(sketch, "E254", {"points": [v(45.12, 8.65) * mm, v(45.12, 8.65) * mm, v(45.12, 8.65) * mm, v(45.12, 8.65) * mm]});
            skFitSpline(sketch, "E255", {"points": [v(45.12, 8.65) * mm, v(45.12, 8.65) * mm, v(45.12, 8.65) * mm, v(45.12, 8.65) * mm]});
            skFitSpline(sketch, "E256", {"points": [v(45.12, 8.65) * mm, v(49.3, 3.48) * mm, v(53.67, 0.94) * mm, v(58.35, 0.4) * mm]});
            skFitSpline(sketch, "E257", {"points": [v(58.35, 0.4) * mm, v(63.04, -0.15) * mm, v(67.61, 0.9) * mm, v(73.56, 1.7) * mm]});
            skFitSpline(sketch, "E258", {"points": [v(73.56, 1.7) * mm, v(79.57, 2.49) * mm, v(83.82, 2.7) * mm, v(87.61, 4.4) * mm]});
            skFitSpline(sketch, "E259", {"points": [v(87.61, 4.4) * mm, v(91.4, 6.1) * mm, v(94, 9.61) * mm, v(95.64, 14.84) * mm]});
            skFitSpline(sketch, "E260", {"points": [v(95.64, 14.84) * mm, v(95.64, 14.84) * mm, v(95.64, 14.84) * mm, v(95.64, 14.84) * mm]});
            skFitSpline(sketch, "E261", {"points": [v(95.64, 14.84) * mm, v(99.66, 27.86) * mm, v(97.37, 44.01) * mm, v(85.68, 53.04) * mm]});
            skFitSpline(sketch, "E262", {"points": [v(85.68, 53.04) * mm, v(85.45, 53.22) * mm, v(85.2, 53.36) * mm, v(84.95, 53.47) * mm]});
            skFitSpline(sketch, "E263", {"points": [v(120.4, 62.28) * mm, v(118.47, 68.53) * mm, v(114.22, 73.06) * mm, v(109.07, 75.94) * mm]});
            skFitSpline(sketch, "E264", {"points": [v(109.07, 75.94) * mm, v(103.93, 78.81) * mm, v(97.9, 80.17) * mm, v(91.82, 80.58) * mm]});
            skFitSpline(sketch, "E265", {"points": [v(91.82, 80.58) * mm, v(90.3, 80.68) * mm, v(88.78, 80.72) * mm, v(87.28, 80.72) * mm]});
            skFitSpline(sketch, "E266", {"points": [v(118.71, 67.05) * mm, v(116.78, 69.83) * mm, v(114.56, 72.01) * mm, v(112.54, 73.32) * mm]});
            skFitSpline(sketch, "E267", {"points": [v(121.5, 54.16) * mm, v(119.23, 52.59) * mm, v(114.3, 55.76) * mm, v(110.45, 61.3) * mm]});
            skFitSpline(sketch, "E268", {"points": [v(110.45, 61.3) * mm, v(106.57, 66.78) * mm, v(105.3, 72.53) * mm, v(107.54, 74.1) * mm]});
            skFitSpline(sketch, "E269", {"points": [v(118.6, 66.97) * mm, v(122.44, 61.48) * mm, v(123.75, 55.72) * mm, v(121.5, 54.16) * mm]});
            skFitSpline(sketch, "E270.trimOffspring", {"points": [v(-56.6, 3.47) * mm, v(-72.13, 13.81) * mm, v(-93.6, 21.85) * mm, v(-102.83, 35.67) * mm]});
            skFitSpline(sketch, "E271.trimOffspring", {"points": [v(71.04, 17.74) * mm, v(62.12, 28.6) * mm, v(62.64, 43.8) * mm, v(72.24, 51.65) * mm]});
            skFitSpline(sketch, "E272.trimOffspring", {"points": [v(72.24, 51.65) * mm, v(81.84, 59.53) * mm, v(96.85, 57.1) * mm, v(105.78, 46.24) * mm]});
            skFitSpline(sketch, "E273.trimOffspring", {"points": [v(80.23, 51.7) * mm, v(89.83, 59.57) * mm, v(104.85, 57.14) * mm, v(113.78, 46.24) * mm]});
            skFitSpline(sketch, "E274.trimOffspring", {"points": [v(71.04, 17.74) * mm, v(62.12, 28.6) * mm, v(62.64, 43.8) * mm, v(72.24, 51.65) * mm]});
            skLineSegment(sketch, "E275", {"start": v(118.71, 67.05) * mm, "end": v(118.6, 66.97) * mm});
            skLineSegment(sketch, "E276.trimOffspring", {"start": v(60.3, 58.55) * mm, "end": v(60.06, 58.77) * mm});
            skFitSpline(sketch, "E277.trimOffspring", {"points": [v(-42.36, -17.82) * mm, v(-42.36, 1.26) * mm, v(-23.01, 16.77) * mm, v(0.9, 16.77) * mm]});
            skFitSpline(sketch, "E278.trimOffspring", {"points": [v(0.9, 16.77) * mm, v(24.8, 16.77) * mm, v(44.15, 1.26) * mm, v(44.15, -17.82) * mm]});
            skFitSpline(sketch, "E279.trimOffspring", {"points": [v(0.9, 16.77) * mm, v(24.8, 16.77) * mm, v(44.15, 1.26) * mm, v(44.15, -17.82) * mm]});
            skFitSpline(sketch, "E280.trimOffspring", {"points": [v(30.55, 5) * mm, v(13.9, 27.7) * mm, v(21.14, 61.3) * mm, v(46.7, 80.04) * mm]});
            skFitSpline(sketch, "E281.trimOffspring", {"points": [v(0.9, 16.77) * mm, v(24.8, 16.77) * mm, v(44.15, 1.26) * mm, v(44.15, -17.82) * mm]});
            skFitSpline(sketch, "E282.trimOffspring", {"points": [v(-83.45, -18.08) * mm, v(-62.8, -2.92) * mm, v(-35.08, -5.53) * mm, v(-21.63, -23.91) * mm]});
            skFitSpline(sketch, "E283.trimOffspring", {"points": [v(24.8, -24.32) * mm, v(38.29, -5.9) * mm, v(65.96, -3.26) * mm, v(86.66, -18.42) * mm]});
            skFitSpline(sketch, "E284.trimOffspring", {"points": [v(-83.45, -18.08) * mm, v(-62.8, -2.92) * mm, v(-35.08, -5.53) * mm, v(-21.63, -23.91) * mm]});
            skFitSpline(sketch, "E285.trimOffspring", {"points": [v(24.8, -24.32) * mm, v(38.29, -5.9) * mm, v(65.96, -3.26) * mm, v(86.66, -18.42) * mm]});
            skLineSegment(sketch, "E286", {"start": v(4.27, -52.79) * mm, "end": v(4.27, -52.3) * mm});
            skLineSegment(sketch, "E287", {"start": v(6.84, -52.78) * mm, "end": v(6.87, -52.09) * mm});
            skLineSegment(sketch, "E288", {"start": v(-9.36, -52.79) * mm, "end": v(-9.36, -51.44) * mm});
            skLineSegment(sketch, "E289", {"start": v(-6.78, -52.79) * mm, "end": v(-6.78, -51.87) * mm});
            skLineSegment(sketch, "E290", {"start": v(4.55, 17.18) * mm, "end": v(4.5, 16.65) * mm});
            skLineSegment(sketch, "E291", {"start": v(7.55, 16.95) * mm, "end": v(7.5, 16.36) * mm});
            skLineSegment(sketch, "E292", {"start": v(-5.98, 16.95) * mm, "end": v(-5.94, 16.34) * mm});
            skLineSegment(sketch, "E293", {"start": v(-2.98, 17.18) * mm, "end": v(-2.94, 16.63) * mm});
            skSolve(sketch);
        }
        {
            var Q0;
            Q0=makeQuery(id+"F0.imprint","IMPRINT",FACE,{"disambiguationData":[TD([[makeQuery(id+"F0.imprint","IMPRINT",EDGE,{"derivedFrom":sQuery(id+"F0.wireOp",EDGE,"E7")}),1.0]])]});
            extrude(context, id + "F1", {"entities" : qUnion([Q0]), "depth" : 5 * mm, "offsetDistance" : 25 * mm});
        }
        {
            var Q0;
            Q0=makeQuery(id+"F0.imprint","IMPRINT",FACE,{"disambiguationData":[TD([[makeQuery(id+"F0.imprint","IMPRINT",EDGE,{"derivedFrom":sQuery(id+"F0.wireOp",EDGE,"E7")}),-1.0]])]});
            extrude(context, id + "F2", {"entities" : qUnion([Q0]), "depth" : 5 * mm, "offsetDistance" : 25 * mm});
        }
    });
